# Revit family: Krill 1.0
name_source: partatom
category: Lighting Fixtures
units: mm (PartAtom-declared; Revit-internal decimal feet)

## family parameters
Always vertical = No
Cut with Voids When Loaded = No
Light Source = No
OmniClass Number = 23.80.70.00
OmniClass Title = Lighting
Part Type = Normal
Room Calculation Point = Yes
Round Connector Dimension = Use Diameter
Shared = No
Work Plane-Based = No

## types (5) — shared parameters
Apparent Load Phase 1 = 1 W
Base = L&L_Anticorodal aluminium
Base bracket = Krill 1.0_Base braket
Body = L&L_Anticorodal aluminium
CRI = CRI>90
Code = -
Control system = -
Cutout dimensions = -
Delivered lumen output = 51 lm (3000K, 350mA, 36°)
Description = Projectors for indoor applications
Energy efficiency class = A A+ A++
Features = -
Geometry = Krill 1.0_mod
H1 = 17 mm
IP = IP40
Joint = L&L_Brass
LED Colour = 3000K (also available: 2700, 4000K - ref. URL Technical sheet)
Length mm = 33 mm  [stored 0.108268 ft]
Lens = L&L_Tempered extra-clear glass
Lumen output at source = 105 lm (3000K, 350mA)
Manufacturer = L&L Luce&Light
Material = body in anticorodal aluminium, joint in brass
Model = Krill 1.0
Mounting = surface mounted (shop windows, display cabinets)
No. and type of led = 1 power LED, 3-step MacAdam, 50 000h L90 B10 (Ta 25°C)
Notes = -
Power = max 1W
Power cables = includes 1.5 m PVC cable HT105° 2x0.20 Ø3.0 mm
Power supply = max 350mA
Power supply unit = not included
not included
not included
Trim = L&L_Black aluminium
URL = https://www.lucelight.it
URL Accessories and power supply units = https://www.lucelight.it
URL Catalogue = -
URL DXF = https://www.lucelight.it
URL Description = https://www.lucelight.it
URL General code = https://www.lucelight.it
URL IES Photometric file = https://www.lucelight.it
URL Image = https://www.lucelight.it
URL Technical sheet = https://www.lucelight.it
Vertical rotation max = 90.00°
Weight kg = 0.035 kg
Width mm = 18 mm  [stored 0.0590551 ft]
Wiring = series
X1 = 105 mm  [stored 0.344488 ft]
zero-valued in all types: Height mm

## per-type parameters (varying)
| type | Light Source | Optics |
| Krill 1.0 J 48° (3000K 1W 350mA) | Light Source 1.0 : J 48° | 48° |
| Krill 1.0 L 36° (3000K 1W 350mA) | Light Source 1.0 : L 36° | 36° |
| Krill 1.0 M 23° (3000K 1W 350mA) | Light Source 1.0 : M 23° | 23° |
| Krill 1.0 W 26°x40° (3000K 1W 350mA) | Light Source 1.0 : W 26°x40° | 26°x40° |
| Krill 1.0 X 40°x26° (3000K 1W 350mA) | Light Source 1.0 : X 40°x26° | 40°x26° |

note: [stored X ft] marks values corroborated as IEEE doubles in the binary element streams (Revit-internal decimal feet)

## geometry (parser evidence)
native form markers: Blend x2, Sweep x12
no freeform markers — native parametric forms only
